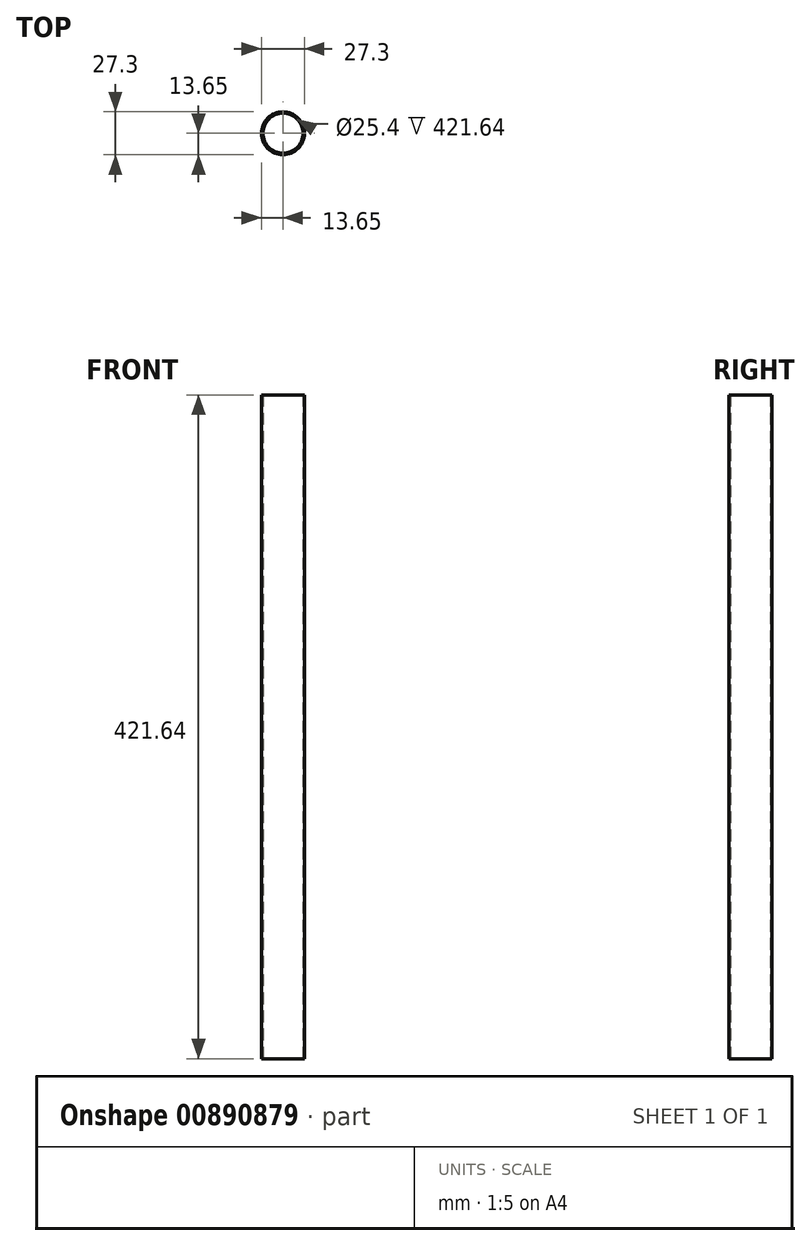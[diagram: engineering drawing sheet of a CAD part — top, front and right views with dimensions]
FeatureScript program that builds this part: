
annotation { "Feature Type Name" : "Feature", "Feature Type Description" : "" }
export const myFeature = defineFeature(function(context is Context, id is Id, definition is map)
    precondition{}
    {
        {
            var Q0;
            Q0=qCreatedBy(makeId("Top.planeOp"),FACE);
            var sketch = newSketch(context, id + "F0", { "sketchPlane" : qUnion([Q0])});
            skCircle(sketch, "E0", {"center": v(0, 0) * mm, "radius": 12.7 * mm});
            skCircle(sketch, "E1", {"center": v(0, 0) * mm, "radius": 13.65 * mm});
            skSolve(sketch);
        }
        {
            var Q0;
            Q0=makeQuery(id+"F0.imprint","IMPRINT",FACE,{"disambiguationData":[TD([[makeQuery(id+"F0.imprint","IMPRINT",EDGE,{"derivedFrom":sQuery(id+"F0.wireOp",EDGE,"E0")}),-1.0]])]});
            extrude(context, id + "F1", {"entities" : qUnion([Q0]), "depth" : 421.64 * mm, "offsetDistance" : 25.4 * mm});
        }
    });
